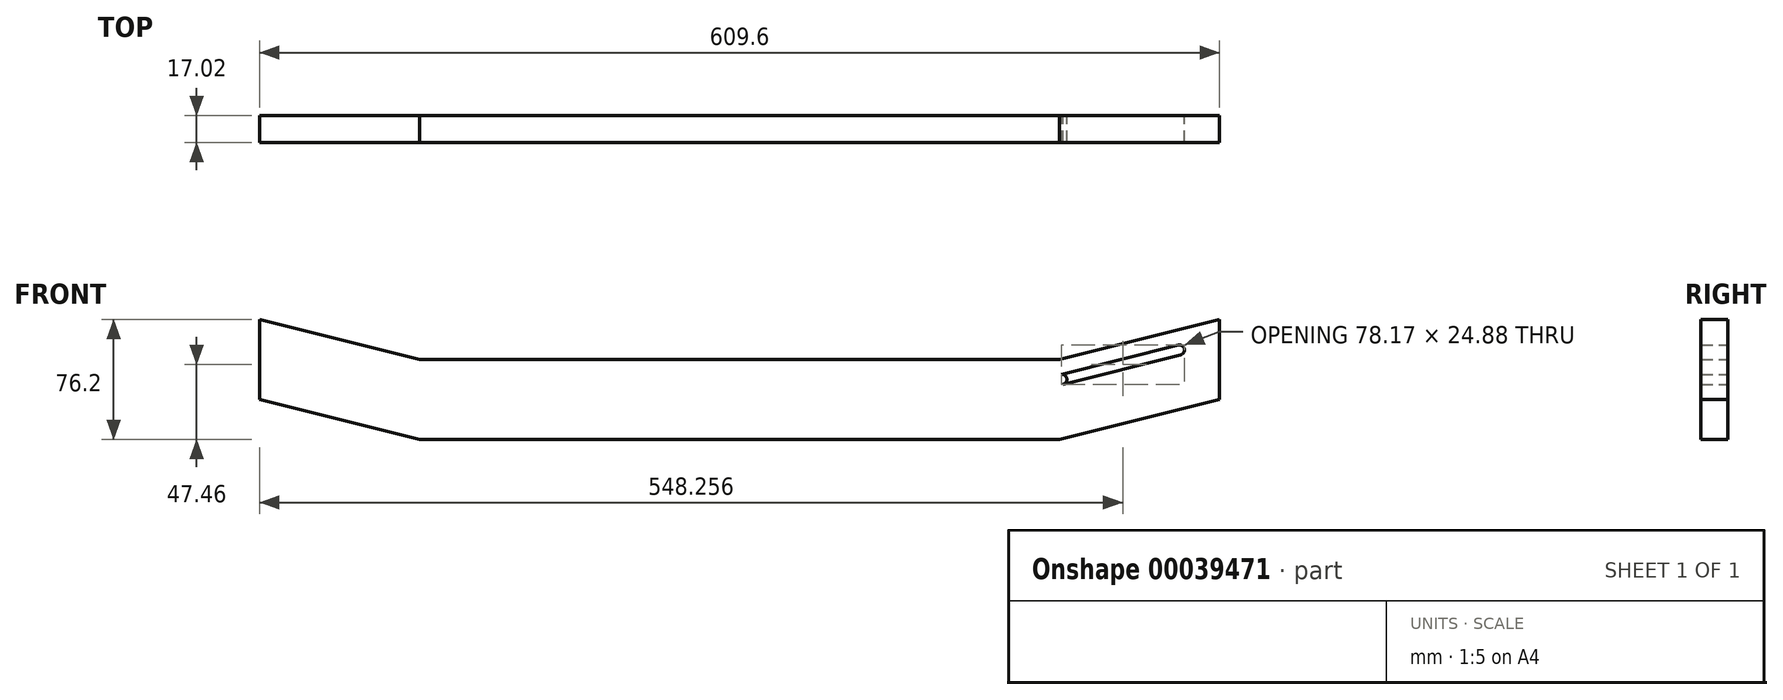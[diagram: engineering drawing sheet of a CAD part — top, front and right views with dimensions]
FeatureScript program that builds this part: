
annotation { "Feature Type Name" : "Feature", "Feature Type Description" : "" }
export const myFeature = defineFeature(function(context is Context, id is Id, definition is map)
    precondition{}
    {
        {
            var Q0;
            Q0=qCreatedBy(makeId("Front.planeOp"),FACE);
            var sketch = newSketch(context, id + "F0", { "sketchPlane" : qUnion([Q0])});
            skLineSegment(sketch, "E0.rect.bottom", {"start": v(304.8, 50.8) * mm, "end": v(-304.8, 50.8) * mm});
            skLineSegment(sketch, "E0.rect.top", {"start": v(304.8, -50.8) * mm, "end": v(-304.8, -50.8) * mm});
            skLineSegment(sketch, "E0.rect.left", {"start": v(304.8, 50.8) * mm, "end": v(304.8, -50.8) * mm});
            skLineSegment(sketch, "E0.rect.right", {"start": v(-304.8, 50.8) * mm, "end": v(-304.8, -50.8) * mm});
            skPoint(sketch, "E0.rect.middle", {"position": v(0, 0) * mm});
            skLineSegment(sketch, "E1", {"start": v(-203.2, 25.4) * mm, "end": v(203.2, 25.4) * mm});
            skLineSegment(sketch, "E2", {"start": v(0, -168.47) * mm, "end": v(0, 168.47) * mm, "construction": true});
            skPoint(sketch, "E3", {"position": v(0, 25.4) * mm});
            skLineSegment(sketch, "E4", {"start": v(-372.38, 0) * mm, "end": v(372.38, 0) * mm, "construction": true});
            skLineSegment(sketch, "E5.MirrorCS", {"start": v(-203.2, -25.4) * mm, "end": v(203.2, -25.4) * mm});
            skLineSegment(sketch, "E6", {"start": v(-304.8, 50.8) * mm, "end": v(-203.2, 25.4) * mm});
            skLineSegment(sketch, "E7", {"start": v(-304.8, 0) * mm, "end": v(-203.2, -25.4) * mm});
            skLineSegment(sketch, "E8", {"start": v(203.2, 25.4) * mm, "end": v(304.8, 50.8) * mm});
            skLineSegment(sketch, "E9", {"start": v(203.2, -25.4) * mm, "end": v(304.8, 0) * mm});
            skLineSegment(sketch, "E10.0", {"start": v(204.76, 12.7) * mm, "end": v(279.4, 31.36) * mm, "construction": true});
            skLineSegment(sketch, "E10.1", {"start": v(-204.76, 12.7) * mm, "end": v(204.76, 12.7) * mm, "construction": true});
            skLineSegment(sketch, "E10.2", {"start": v(-279.4, 31.36) * mm, "end": v(-204.76, 12.7) * mm, "construction": true});
            skArc(sketch, "E11.0.startCap", {"start": v(205.53, 9.62) * mm, "mid": v(201.68, 11.93) * mm, "end": v(204, 15.78) * mm});
            skArc(sketch, "E11.0.endCap", {"start": v(278.63, 34.44) * mm, "mid": v(282.48, 32.13) * mm, "end": v(280.17, 28.28) * mm});
            skLineSegment(sketch, "E11.0.left", {"start": v(204, 15.78) * mm, "end": v(278.63, 34.44) * mm});
            skLineSegment(sketch, "E11.0.right", {"start": v(205.53, 9.62) * mm, "end": v(280.17, 28.28) * mm});
            skArc(sketch, "E11.1.startCap", {"start": v(-204.76, 9.52) * mm, "mid": v(-207.94, 12.7) * mm, "end": v(-204.76, 15.87) * mm});
            skArc(sketch, "E11.1.endCap", {"start": v(204.76, 15.87) * mm, "mid": v(207.94, 12.7) * mm, "end": v(204.76, 9.52) * mm});
            skLineSegment(sketch, "E11.1.left", {"start": v(-204.76, 15.87) * mm, "end": v(204.76, 15.87) * mm});
            skLineSegment(sketch, "E11.1.right", {"start": v(-204.76, 9.52) * mm, "end": v(204.76, 9.52) * mm});
            skArc(sketch, "E11.2.startCap", {"start": v(-280.17, 28.28) * mm, "mid": v(-282.48, 32.13) * mm, "end": v(-278.63, 34.44) * mm});
            skArc(sketch, "E11.2.endCap", {"start": v(-204, 15.78) * mm, "mid": v(-201.68, 11.93) * mm, "end": v(-205.53, 9.62) * mm});
            skLineSegment(sketch, "E11.2.left", {"start": v(-278.63, 34.44) * mm, "end": v(-204, 15.78) * mm});
            skLineSegment(sketch, "E11.2.right", {"start": v(-280.17, 28.28) * mm, "end": v(-205.53, 9.62) * mm});
            skSolve(sketch);
        }
        {
            var Q0;
            Q0=makeQuery(id+"F0.imprint","IMPRINT",FACE,{"disambiguationData":[TD([[makeQuery(id+"F0.imprint","IMPRINT",EDGE,{"derivedFrom":sQuery(id+"F0.wireOp",EDGE,"E1")}),-1.0]])]});
            var Q1;
            {var subQ0=sQuery(id+"F0.wireOp",EDGE,"E11.1.startCap");Q1=makeQuery(id+"F0.imprint","IMPRINT",FACE,{"disambiguationData":[TD([[makeQuery(id+"F0.imprint","IMPRINT",EDGE,{"derivedFrom":subQ0}),1.0]])]});}
            var Q2;
            {var subQ0=sQuery(id+"F0.wireOp",EDGE,"E11.0.startCap");Q2=makeQuery(id+"F0.imprint","IMPRINT",FACE,{"disambiguationData":[TD([[makeQuery(id+"F0.imprint","IMPRINT",EDGE,{"derivedFrom":subQ0}),1.0]])]});}
            var Q3;
            {var subQ5=sQuery(id+"F0.wireOp",EDGE,"E11.0.endCap");Q3=makeQuery(id+"F0.imprint","IMPRINT",FACE,{"disambiguationData":[TD([[makeQuery(id+"F0.imprint","IMPRINT",EDGE,{"derivedFrom":subQ5}),-1.0]])]});}
            var Q4;
            {var subQ5=sQuery(id+"F0.wireOp",EDGE,"E11.0.startCap");Q4=makeQuery(id+"F0.imprint","IMPRINT",FACE,{"disambiguationData":[TD([[makeQuery(id+"F0.imprint","IMPRINT",EDGE,{"derivedFrom":subQ5}),-1.0]])]});}
            var Q5;
            {var subQ5=sQuery(id+"F0.wireOp",EDGE,"E11.1.startCap");Q5=makeQuery(id+"F0.imprint","IMPRINT",FACE,{"disambiguationData":[TD([[makeQuery(id+"F0.imprint","IMPRINT",EDGE,{"derivedFrom":subQ5}),-1.0]])]});}
            extrude(context, id + "F1", {"entities" : qUnion([Q0, Q1, Q2, Q3, Q4, Q5]), "depth" : 25.4 * mm});
        }
        {
            var Q0;
            {var subQ0=sQuery(id+"F0.wireOp",EDGE,"E11.1.startCap");Q0=makeQuery(id+"F0.imprint","IMPRINT",FACE,{"disambiguationData":[TD([[makeQuery(id+"F0.imprint","IMPRINT",EDGE,{"derivedFrom":subQ0}),1.0]])]});}
            var Q1;
            {var subQ0=sQuery(id+"F0.wireOp",EDGE,"E11.0.startCap");Q1=makeQuery(id+"F0.imprint","IMPRINT",FACE,{"disambiguationData":[TD([[makeQuery(id+"F0.imprint","IMPRINT",EDGE,{"derivedFrom":subQ0}),1.0]])]});}
            var Q2;
            {var subQ5=sQuery(id+"F0.wireOp",EDGE,"E11.0.endCap");Q2=makeQuery(id+"F0.imprint","IMPRINT",FACE,{"disambiguationData":[TD([[makeQuery(id+"F0.imprint","IMPRINT",EDGE,{"derivedFrom":subQ5}),-1.0]])]});}
            var Q3;
            {var subQ5=sQuery(id+"F0.wireOp",EDGE,"E11.0.startCap");Q3=makeQuery(id+"F0.imprint","IMPRINT",FACE,{"disambiguationData":[TD([[makeQuery(id+"F0.imprint","IMPRINT",EDGE,{"derivedFrom":subQ5}),-1.0]])]});}
            var Q4;
            {var subQ5=sQuery(id+"F0.wireOp",EDGE,"E11.1.startCap");Q4=makeQuery(id+"F0.imprint","IMPRINT",FACE,{"disambiguationData":[TD([[makeQuery(id+"F0.imprint","IMPRINT",EDGE,{"derivedFrom":subQ5}),-1.0]])]});}
            extrude(context, id + "F2", {"entities" : qUnion([Q0, Q1, Q2, Q3, Q4]), "operationType" : NewBodyOperationType.REMOVE, "depth" : 8.38 * mm});
        }
    });
